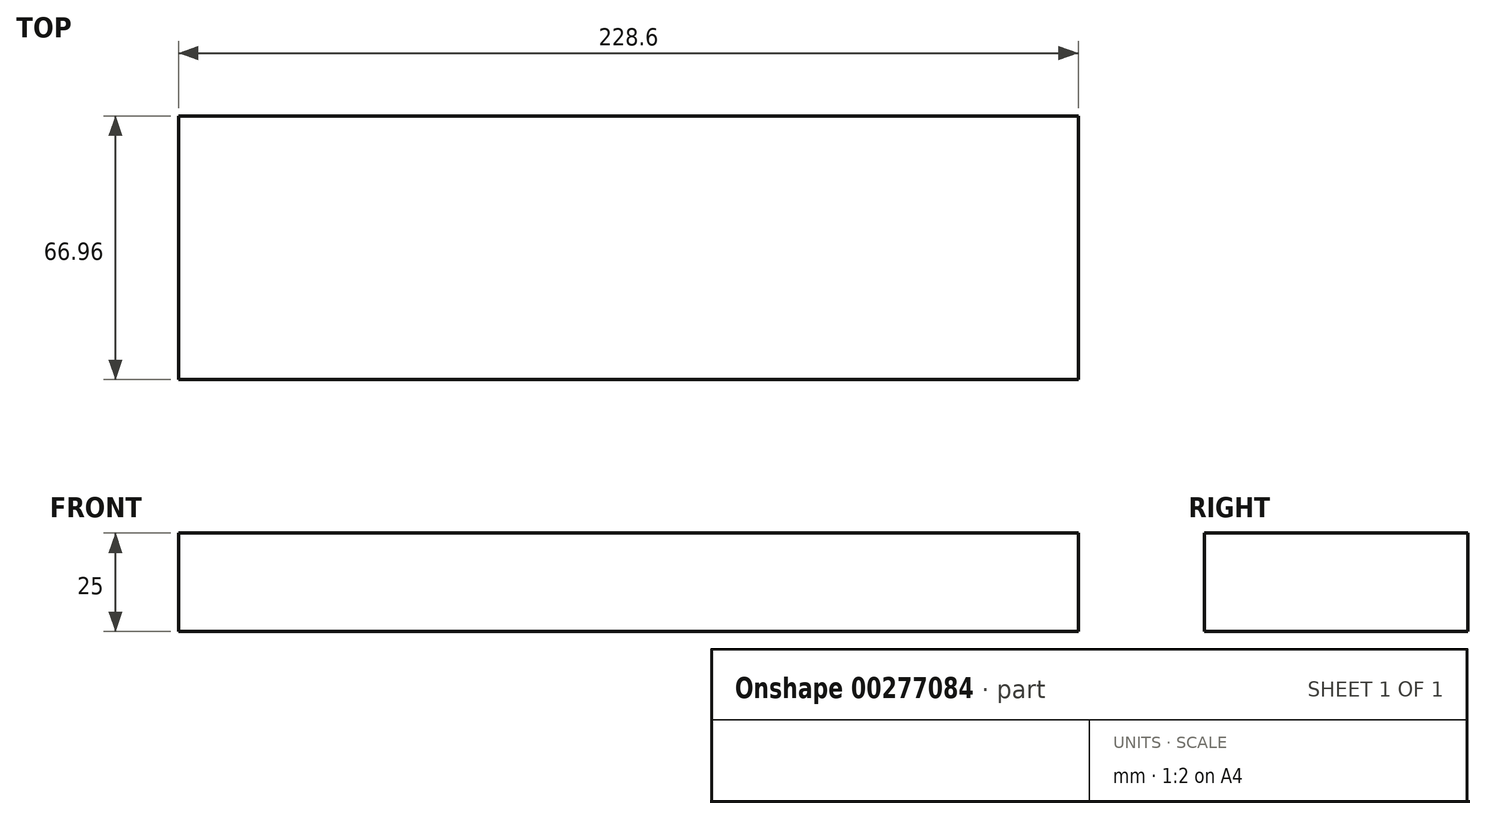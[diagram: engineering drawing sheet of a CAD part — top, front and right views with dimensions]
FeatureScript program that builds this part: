
annotation { "Feature Type Name" : "Feature", "Feature Type Description" : "" }
export const myFeature = defineFeature(function(context is Context, id is Id, definition is map)
    precondition{}
    {
        {
            var Q0;
            Q0=qCreatedBy(makeId("Top.planeOp"),FACE);
            var sketch = newSketch(context, id + "F0", { "sketchPlane" : qUnion([Q0])});
            skLineSegment(sketch, "E0.bottom", {"start": v(-114.3, 33.48) * mm, "end": v(114.3, 33.48) * mm});
            skLineSegment(sketch, "E0.top", {"start": v(-114.3, -33.48) * mm, "end": v(114.3, -33.48) * mm});
            skLineSegment(sketch, "E0.left", {"start": v(-114.3, 33.48) * mm, "end": v(-114.3, -33.48) * mm});
            skLineSegment(sketch, "E0.right", {"start": v(114.3, 33.48) * mm, "end": v(114.3, -33.48) * mm});
            skPoint(sketch, "E0.middle", {"position": v(0, 0) * mm});
            skSolve(sketch);
        }
        {
            var Q0;
            Q0=makeQuery(id+"F0.imprint","IMPRINT",FACE,{"disambiguationData":[TD([[makeQuery(id+"F0.imprint","IMPRINT",EDGE,{"derivedFrom":sQuery(id+"F0.wireOp",EDGE,"E0.bottom")}),-1.0]])]});
            extrude(context, id + "F1", {"entities" : qUnion([Q0]), "depth" : 25 * mm});
        }
    });
